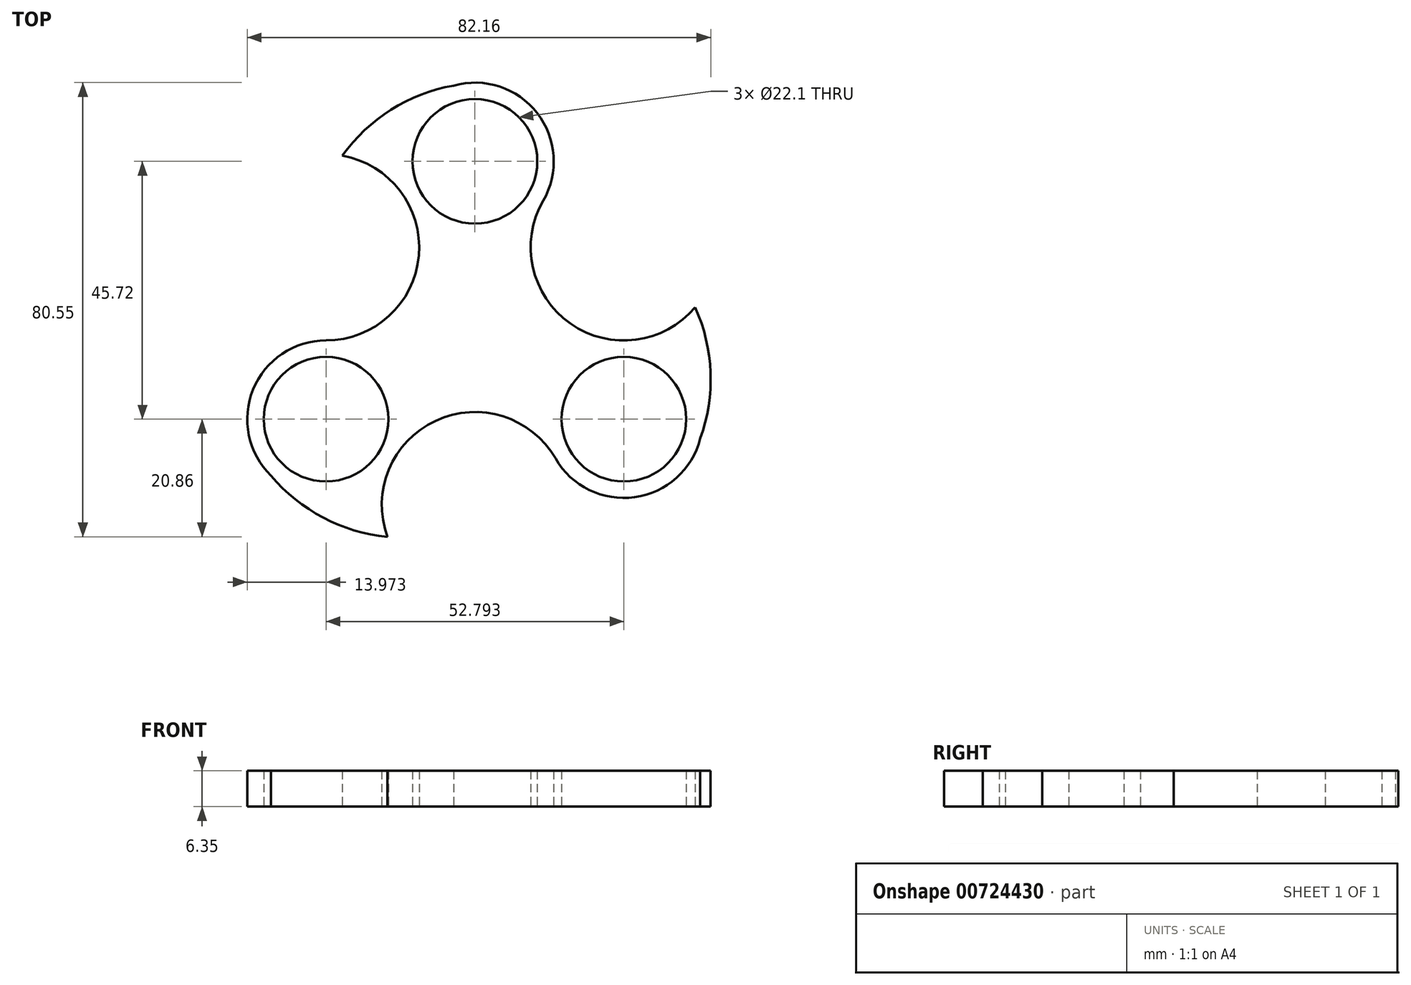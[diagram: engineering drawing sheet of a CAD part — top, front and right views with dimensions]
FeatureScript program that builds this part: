
annotation { "Feature Type Name" : "Feature", "Feature Type Description" : "" }
export const myFeature = defineFeature(function(context is Context, id is Id, definition is map)
    precondition{}
    {
        {
            var Q0;
            Q0=qCreatedBy(makeId("Top.planeOp"),FACE);
            var sketch = newSketch(context, id + "F0", { "sketchPlane" : qUnion([Q0])});
            skLineSegment(sketch, "E0", {"start": v(0, 0) * mm, "end": v(0, 30.48) * mm});
            skCircle(sketch, "E1", {"center": v(0, 30.48) * mm, "radius": 11.05 * mm});
            skCircle(sketch, "E2", {"center": v(0, 30.48) * mm, "radius": 13.97 * mm});
            skLineSegment(sketch, "E3.1.0", {"start": v(0, 0) * mm, "end": v(-26.4, -15.24) * mm});
            skCircle(sketch, "E3.1.1", {"center": v(-26.4, -15.24) * mm, "radius": 11.05 * mm});
            skLineSegment(sketch, "E3.2.0", {"start": v(0, 0) * mm, "end": v(26.4, -15.24) * mm});
            skCircle(sketch, "E3.2.1", {"center": v(26.4, -15.24) * mm, "radius": 11.05 * mm});
            skPoint(sketch, "E3.center", {"position": v(0, 0) * mm});
            skCircle(sketch, "E4.1.0", {"center": v(-26.4, -15.24) * mm, "radius": 13.97 * mm});
            skCircle(sketch, "E4.2.0", {"center": v(26.4, -15.24) * mm, "radius": 13.97 * mm});
            skLineSegment(sketch, "E5", {"start": v(26.4, -15.24) * mm, "end": v(0, 0) * mm});
            skLineSegment(sketch, "E6", {"start": v(-12.13, 6.92) * mm, "end": v(-26.47, 15.1) * mm});
            skArc(sketch, "E7", {"start": v(-27.85, -1.35) * mm, "mid": v(-26.43, -1.4) * mm, "end": v(-25.01, -1.34) * mm});
            skLineSegment(sketch, "E8", {"start": v(0, 0) * mm, "end": v(0, -30.48) * mm});
            skLineSegment(sketch, "E9", {"start": v(0, 0) * mm, "end": v(26.4, 15.24) * mm});
            skArc(sketch, "E10", {"start": v(12.1, 23.5) * mm, "mid": v(12.1, 6.98) * mm, "end": v(26.4, -1.27) * mm});
            skArc(sketch, "E11.1.0", {"start": v(-26.4, -1.27) * mm, "mid": v(-12.1, 6.99) * mm, "end": v(-12.1, 23.5) * mm});
            skArc(sketch, "E11.2.0", {"start": v(14.3, -22.22) * mm, "mid": v(0, -13.97) * mm, "end": v(-14.3, -22.22) * mm});
            skPoint(sketch, "E12", {"position": v(37.85, -23.23) * mm});
            skArc(sketch, "E13", {"start": v(1.2, 44.4) * mm, "mid": v(0, 44.41) * mm, "end": v(-1.2, 44.4) * mm});
            skPoint(sketch, "E14", {"position": v(44.41, 0) * mm});
            skArc(sketch, "E15.trimOffspring", {"start": v(-39.05, -21.17) * mm, "mid": v(-38.46, -22.2) * mm, "end": v(-37.85, -23.23) * mm});
            skArc(sketch, "E16", {"start": v(14.3, -22.22) * mm, "mid": v(-6.97, -15.51) * mm, "end": v(-15.52, -36.1) * mm});
            skPoint(sketch, "E17", {"position": v(-15.52, -36.1) * mm});
            skPoint(sketch, "E18.orphan", {"position": v(-22.2, -38.46) * mm});
            skArc(sketch, "E19.1.0", {"start": v(12.1, 23.5) * mm, "mid": v(16.92, 1.72) * mm, "end": v(39.03, 4.6) * mm});
            skArc(sketch, "E19.2.0", {"start": v(-26.4, -1.27) * mm, "mid": v(-9.95, 13.79) * mm, "end": v(-23.5, 31.5) * mm});
            skArc(sketch, "E20", {"start": v(37.85, -23.23) * mm, "mid": v(41.76, -9.45) * mm, "end": v(39.03, 4.6) * mm});
            skArc(sketch, "E21.1.1", {"start": v(1.2, 44.4) * mm, "mid": v(-12.7, 40.9) * mm, "end": v(-23.5, 31.5) * mm});
            skArc(sketch, "E21.2.1", {"start": v(-39.05, -21.17) * mm, "mid": v(-29.07, -31.44) * mm, "end": v(-15.52, -36.1) * mm});
            skSolve(sketch);
        }
        {
            var Q0;
            Q0 = qSketchRegion(id + "F0", true);
            extrude(context, id + "F1", {"entities" : qUnion([Q0]), "depth" : 6.35 * mm, "offsetDistance" : 25.4 * mm});
        }
    });
